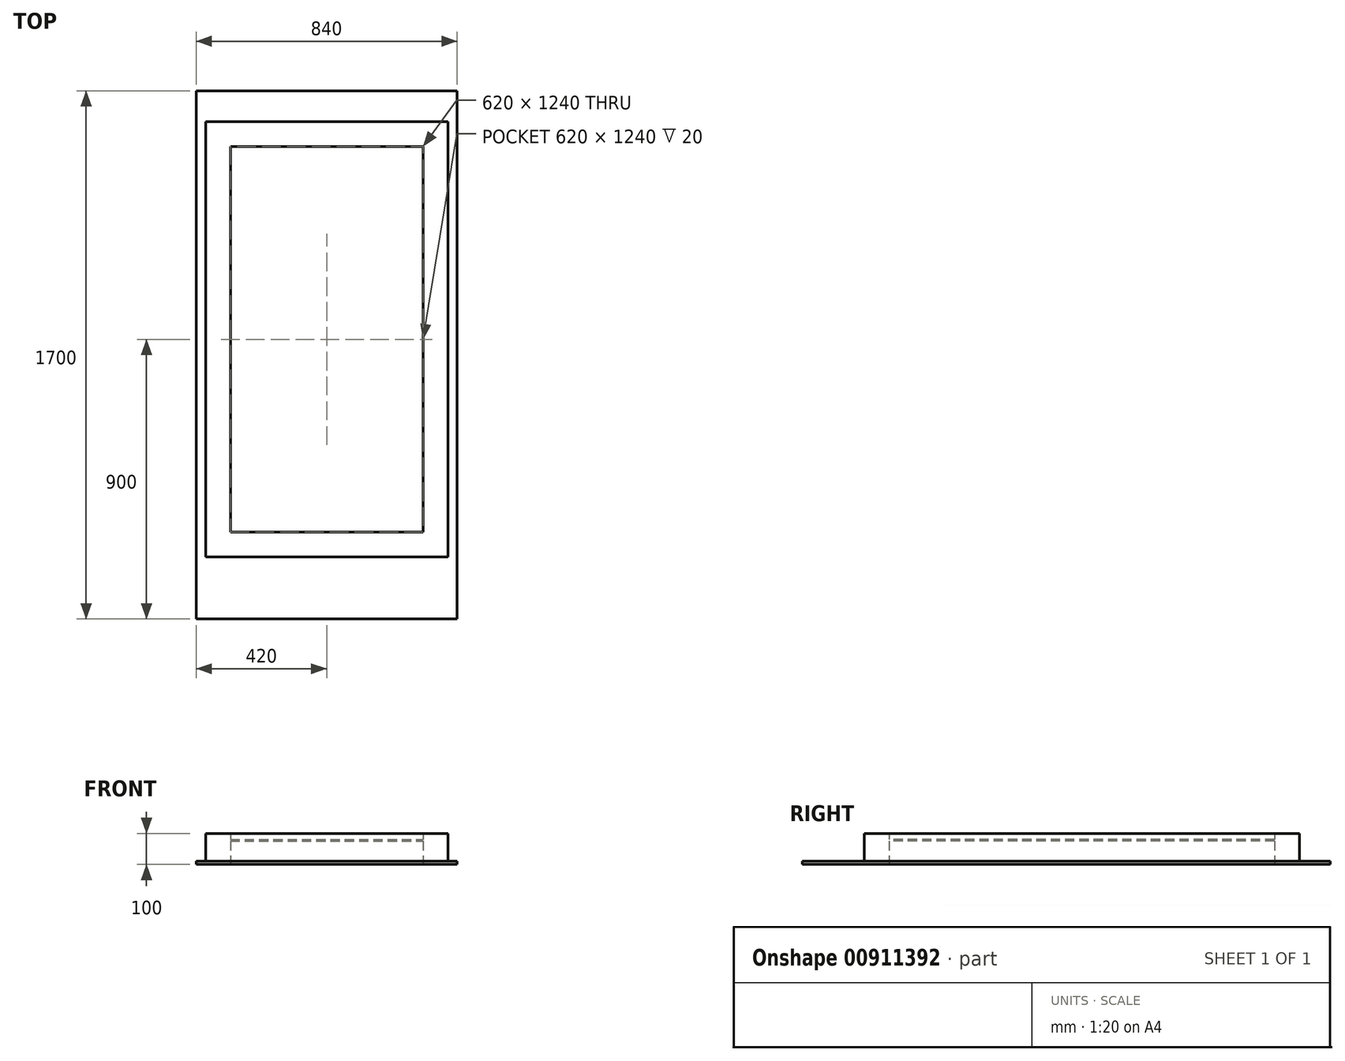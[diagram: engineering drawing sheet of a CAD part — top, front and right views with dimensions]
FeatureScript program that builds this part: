
annotation { "Feature Type Name" : "Feature", "Feature Type Description" : "" }
export const myFeature = defineFeature(function(context is Context, id is Id, definition is map)
    precondition{}
    {
        {
            var Q0;
            Q0=qCreatedBy(makeId("Top.planeOp"),FACE);
            var sketch = newSketch(context, id + "F0", { "sketchPlane" : qUnion([Q0])});
            skLineSegment(sketch, "E0.bottom", {"start": v(0, 0) * mm, "end": v(780, 0) * mm});
            skLineSegment(sketch, "E0.top", {"start": v(0, 1400) * mm, "end": v(780, 1400) * mm});
            skLineSegment(sketch, "E0.left", {"start": v(0, 0) * mm, "end": v(0, 1400) * mm});
            skLineSegment(sketch, "E0.right", {"start": v(780, 0) * mm, "end": v(780, 1400) * mm});
            skLineSegment(sketch, "E1.bottom", {"start": v(80, 1320) * mm, "end": v(700, 1320) * mm});
            skLineSegment(sketch, "E1.top", {"start": v(80, 80) * mm, "end": v(700, 80) * mm});
            skLineSegment(sketch, "E1.left", {"start": v(80, 1320) * mm, "end": v(80, 80) * mm});
            skLineSegment(sketch, "E1.right", {"start": v(700, 1320) * mm, "end": v(700, 80) * mm});
            skSolve(sketch);
        }
        {
            var Q0;
            Q0 = qSketchRegion(id + "F0", true);
            extrude(context, id + "F1", {"entities" : qUnion([Q0]), "depth" : 100 * mm, "offsetDistance" : 25 * mm});
        }
        {
            var Q0;
            Q0=makeQuery(id+"F1.opExtrude","CAP_FACE",FACE,{"disambiguationData":[OSD([sQuery(id+"F0.wireOp",EDGE,"E0.bottom"),sQuery(id+"F0.wireOp",EDGE,"E0.top"),sQuery(id+"F0.wireOp",EDGE,"E0.left"),sQuery(id+"F0.wireOp",EDGE,"E0.right"),sQuery(id+"F0.wireOp",EDGE,"E1.bottom"),sQuery(id+"F0.wireOp",EDGE,"E1.top"),sQuery(id+"F0.wireOp",EDGE,"E1.left"),sQuery(id+"F0.wireOp",EDGE,"E1.right")])],"isStart":true});
            var sketch = newSketch(context, id + "F2", { "sketchPlane" : qUnion([Q0])});
            skLineSegment(sketch, "E2.bottom", {"start": v(810, -1500) * mm, "end": v(-30, -1500) * mm});
            skLineSegment(sketch, "E2.top", {"start": v(810, 200) * mm, "end": v(-30, 200) * mm});
            skLineSegment(sketch, "E2.left", {"start": v(810, -1500) * mm, "end": v(810, 200) * mm});
            skLineSegment(sketch, "E2.right", {"start": v(-30, -1500) * mm, "end": v(-30, 200) * mm});
            skLineSegment(sketch, "E3.bottom", {"start": v(780, -1400) * mm, "end": v(0, -1400) * mm});
            skLineSegment(sketch, "E3.top", {"start": v(780, 0) * mm, "end": v(0, 0) * mm});
            skLineSegment(sketch, "E3.left", {"start": v(780, -1400) * mm, "end": v(780, 0) * mm});
            skLineSegment(sketch, "E3.right", {"start": v(0, -1400) * mm, "end": v(0, 0) * mm});
            skSolve(sketch);
        }
        {
            var Q0;
            Q0 = qSketchRegion(id + "F2", true);
            extrude(context, id + "F3", {"entities" : qUnion([Q0]), "operationType" : NewBodyOperationType.ADD, "oppositeDirection" : true, "depth" : 10 * mm, "offsetDistance" : 25 * mm});
        }
        {
            var Q0;
            Q0=makeQuery(id+"F1.opExtrude","CAP_FACE",FACE,{"disambiguationData":[OSD([sQuery(id+"F0.wireOp",EDGE,"E0.bottom"),sQuery(id+"F0.wireOp",EDGE,"E0.top"),sQuery(id+"F0.wireOp",EDGE,"E0.left"),sQuery(id+"F0.wireOp",EDGE,"E0.right"),sQuery(id+"F0.wireOp",EDGE,"E1.bottom"),sQuery(id+"F0.wireOp",EDGE,"E1.top"),sQuery(id+"F0.wireOp",EDGE,"E1.left"),sQuery(id+"F0.wireOp",EDGE,"E1.right")])],"isStart":false});
            cPlane(context, id + "F4", {"entities" : qUnion([Q0]), "cplaneType" : CPlaneType.OFFSET, "offset" : 25 * mm, "oppositeDirection" : true, "width" : 150 * mm, "height" : 150 * mm});
        }
        {
            var Q0;
            Q0=qCreatedBy(id+"F4.planeOp",FACE);
            var sketch = newSketch(context, id + "F5", { "sketchPlane" : qUnion([Q0])});
            skLineSegment(sketch, "E4.bottom", {"start": v(80, 1320) * mm, "end": v(700, 1320) * mm});
            skLineSegment(sketch, "E4.top", {"start": v(80, 80) * mm, "end": v(700, 80) * mm});
            skLineSegment(sketch, "E4.left", {"start": v(80, 1320) * mm, "end": v(80, 80) * mm});
            skLineSegment(sketch, "E4.right", {"start": v(700, 1320) * mm, "end": v(700, 80) * mm});
            skSolve(sketch);
        }
        {
            var Q0;
            Q0 = qSketchRegion(id + "F5", true);
            extrude(context, id + "F6", {"entities" : qUnion([Q0]), "operationType" : NewBodyOperationType.ADD, "depth" : 5 * mm, "offsetDistance" : 25 * mm});
        }
    });
